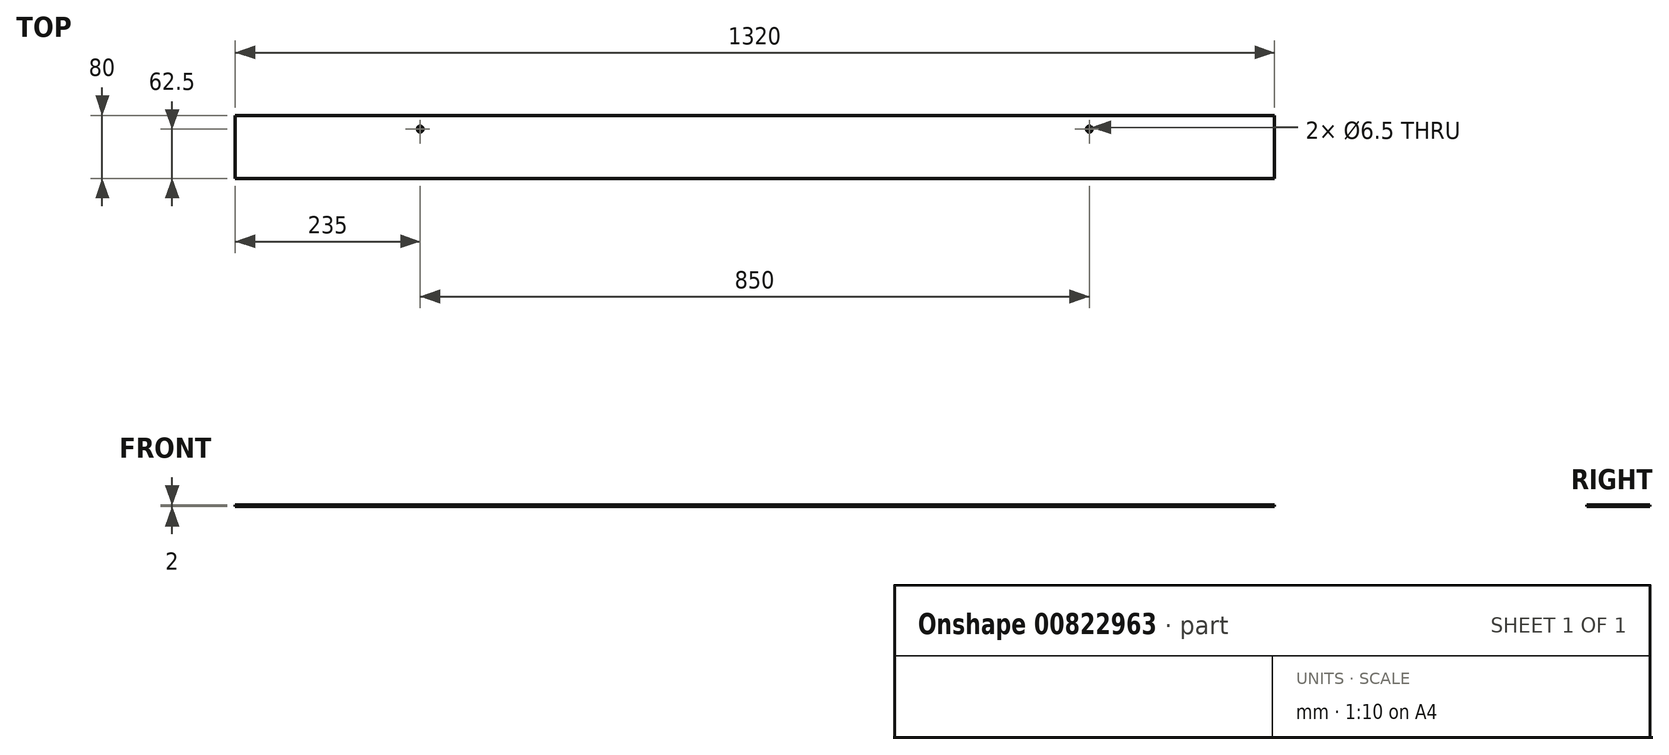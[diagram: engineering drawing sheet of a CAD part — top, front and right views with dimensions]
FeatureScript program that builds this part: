
annotation { "Feature Type Name" : "Feature", "Feature Type Description" : "" }
export const myFeature = defineFeature(function(context is Context, id is Id, definition is map)
    precondition{}
    {
        {
            var Q0;
            Q0=qCreatedBy(makeId("Top.planeOp"),FACE);
            var sketch = newSketch(context, id + "F0", { "sketchPlane" : qUnion([Q0])});
            skLineSegment(sketch, "E0.bottom", {"start": v(-660, -40) * mm, "end": v(660, -40) * mm});
            skLineSegment(sketch, "E0.top", {"start": v(-660, 40) * mm, "end": v(660, 40) * mm});
            skLineSegment(sketch, "E0.left", {"start": v(-660, -40) * mm, "end": v(-660, 40) * mm});
            skLineSegment(sketch, "E0.right", {"start": v(660, -40) * mm, "end": v(660, 40) * mm});
            skPoint(sketch, "E0.middle", {"position": v(0, 0) * mm});
            skLineSegment(sketch, "E1", {"start": v(0, 0) * mm, "end": v(0, 139.06) * mm, "construction": true});
            skCircle(sketch, "E2", {"center": v(-425, 22.5) * mm, "radius": 3.25 * mm});
            skCircle(sketch, "E3.MirrorC", {"center": v(425, 22.5) * mm, "radius": 3.25 * mm});
            skSolve(sketch);
        }
        {
            var Q0;
            Q0 = qSketchRegion(id + "F0", true);
            extrude(context, id + "F1", {"entities" : qUnion([Q0]), "depth" : 2 * mm, "offsetDistance" : 25 * mm});
        }
        {
            var Q0;
            Q0=makeQuery(id+"F1.opExtrude","SWEPT_FACE",FACE,{"disambiguationData":[OSD([sQuery(id+"F0.wireOp",EDGE,"E2")])]});
            var Q1;
            Q1=makeQuery(id+"F1.opExtrude","SWEPT_FACE",FACE,{"disambiguationData":[OSD([sQuery(id+"F0.wireOp",EDGE,"E3.MirrorC")])]});
            chamfer(context, id + "F2", {"entities" : qUnion([Q0, Q1]), "width" : 0.5 * mm, "tangentPropagation" : true});
        }
    });
